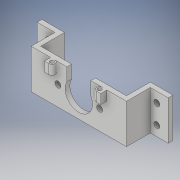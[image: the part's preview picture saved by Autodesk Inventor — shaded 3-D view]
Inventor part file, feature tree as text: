
AUTODESK INVENTOR PART (.ipt)
format: ipt  version: 2019 (Build 230136000, 136)  size: 228,352 bytes
history: native  units: mm
features: extrude x11, sketch x11
ambient origin geometry x8: Origin, YZ Plane, XZ Plane, XY Plane, X Axis, Y Axis, Z Axis, Center Point
bodies: Solid1 (feature_tree)
feature tree (22):
  extrude  "Extrusion1"  Depth=19.0mm
  extrude  "Extrusion2"  Depth=24.0mm
  extrude  "Extrusion3"  Depth=24.0mm
  extrude  "Extrusion4"  Depth=80.0mm
  extrude  "Extrusion5"  Depth=80.0mm
  extrude  "Extrusion6"  Depth=24.0mm
  extrude  "Extrusion7"  Depth=24.0mm
  extrude  "Extrusion8"  Depth=19.0mm
  extrude  "Extrusion9"  Depth=19.0mm
  extrude  "Extrusion10"  Depth=33.0mm TaperAngle=0.0deg
  extrude  "Extrusion11"  Depth=10.82mm
  sketch  "Sketch1"  dims[d0=33.0mm d1=19.0mm]
  sketch  "Sketch2"  dims[d2=4.0mm d3=0.0mm d4=24.0mm]
  sketch  "Sketch3"  dims[d5=4.0mm d6=24.0mm]
  sketch  "Sketch4"  dims[d7=33.0mm d8=0.0mm d9=80.0mm]
  sketch  "Sketch5"  dims[d10=4.0mm d11=80.0mm]
  sketch  "Sketch6"  dims[d12=33.0mm d13=0.0mm d14=24.0mm]
  sketch  "Sketch7"  dims[d15=4.0mm d16=24.0mm]
  sketch  "Sketch8"  dims[d17=33.0mm d18=0.0mm d19=19.0mm]
  sketch  "Sketch9"  dims[d20=4.0mm d21=19.0mm]
  sketch  "Sketch10"  dims[d22=4.0mm d23=33.0mm d24=0.0mm]
  sketch  "Sketch11"  dims[d27=10.82mm d28=10.82mm d30=23.0mm d31=4.0mm d32=0.0mm d35=5.0mm d36=5.0mm d37=4.0mm d38=0.0mm d39=19.0mm d43=5.0mm d44=5.0mm d45=4.0mm d46=0.0mm d49=5.0mm d52=5.0mm d53=4.0mm d54=0.0mm d56=5.2mm d57=6.2mm d58=5.2mm d59=6.2mm d60=2.6mm d61=3.2mm d62=8.0mm d63=0.0mm d64=16.4mm d65=5.2mm d66=6.2mm d67=5.2mm d68=6.2mm d69=2.6mm d70=3.2mm d71=8.0mm d72=0.0mm]
